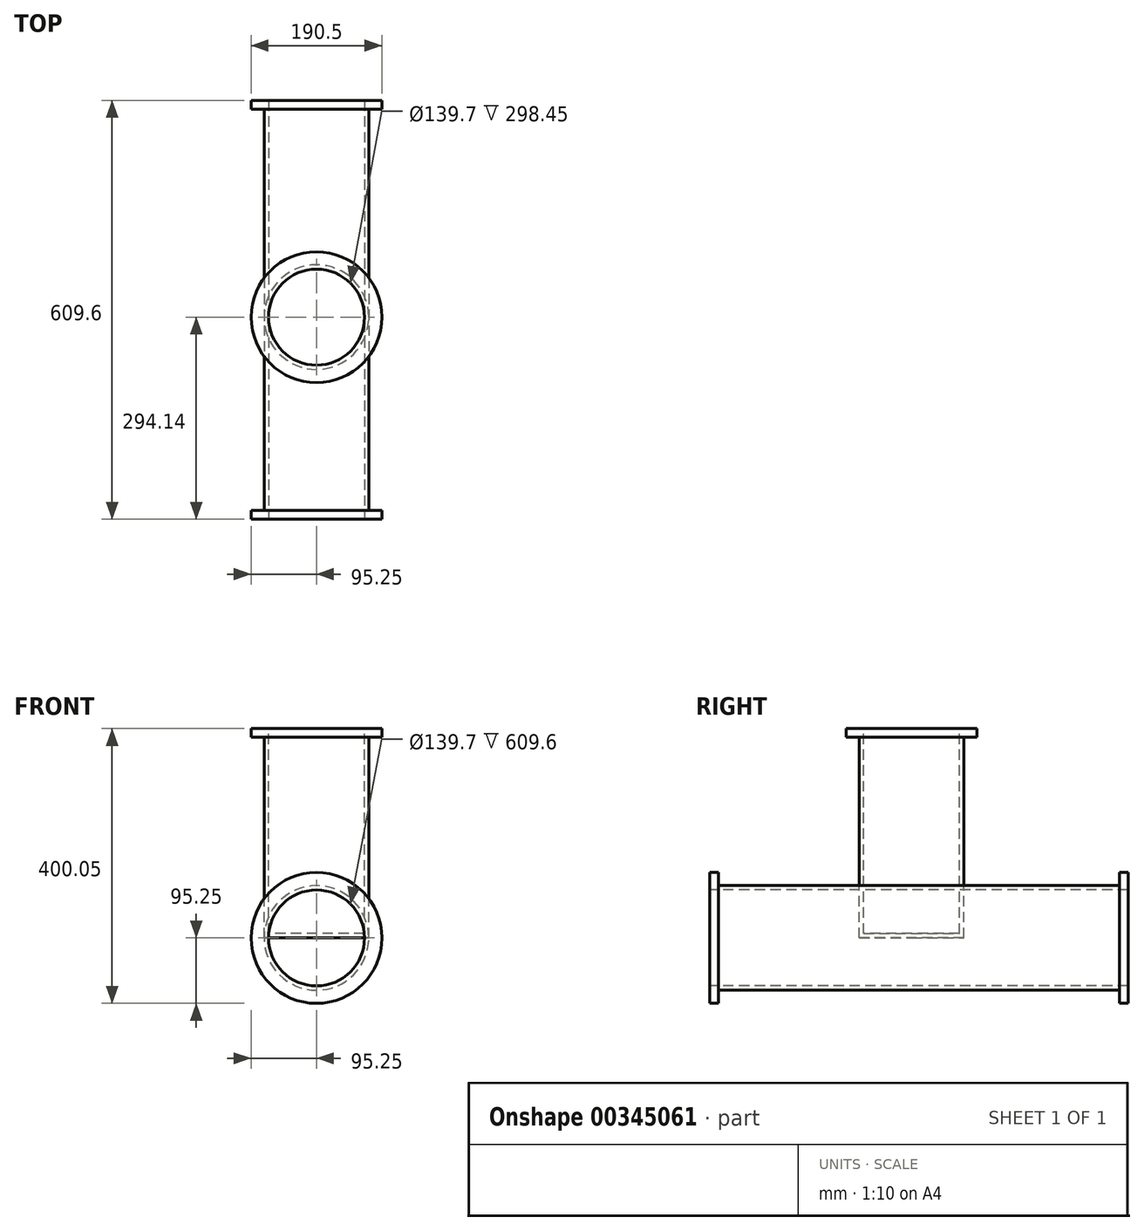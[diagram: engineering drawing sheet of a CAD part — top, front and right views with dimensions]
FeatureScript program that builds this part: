
annotation { "Feature Type Name" : "Feature", "Feature Type Description" : "" }
export const myFeature = defineFeature(function(context is Context, id is Id, definition is map)
    precondition{}
    {
        {
            var Q0;
            Q0=qCreatedBy(makeId("Right.planeOp"),FACE);
            var sketch = newSketch(context, id + "F0", { "sketchPlane" : qUnion([Q0])});
            skLineSegment(sketch, "E0", {"start": v(-294.14, 0) * mm, "end": v(315.46, 0) * mm});
            skLineSegment(sketch, "E1", {"start": v(0, 304.8) * mm, "end": v(0, 0) * mm});
            skSolve(sketch);
        }
        {
            var Q0;
            Q0=sQuery(id+"F0.wireOp",VERTEX,"E0.start");
            var Q1;
            Q1=qCreatedBy(makeId("Front.planeOp"),FACE);
            cPlane(context, id + "F1", {"entities" : qUnion([Q0, Q1]), "cplaneType" : CPlaneType.PLANE_POINT, "offset" : 320.04 * mm, "width" : 152.4 * mm, "height" : 152.4 * mm});
        }
        {
            var Q0;
            Q0=qCreatedBy(id+"F1.planeOp",FACE);
            var sketch = newSketch(context, id + "F2", { "sketchPlane" : qUnion([Q0])});
            skCircle(sketch, "E2", {"center": v(0, 0) * mm, "radius": 76.2 * mm});
            skSolve(sketch);
        }
        {
            var Q0;
            Q0=qCreatedBy(makeId("Top.planeOp"),FACE);
            var Q1;
            Q1=sQuery(id+"F0.wireOp",VERTEX,"E1.start");
            cPlane(context, id + "F3", {"entities" : qUnion([Q0, Q1]), "cplaneType" : CPlaneType.PLANE_POINT, "offset" : 25.4 * mm, "width" : 152.4 * mm, "height" : 152.4 * mm});
        }
        {
            var Q0;
            Q0=qCreatedBy(id+"F3.planeOp",FACE);
            var sketch = newSketch(context, id + "F4", { "sketchPlane" : qUnion([Q0])});
            skCircle(sketch, "E3", {"center": v(0, 0) * mm, "radius": 76.2 * mm});
            skSolve(sketch);
        }
        {
            var Q0;
            Q0=makeQuery(id+"F2.imprint","IMPRINT",FACE,{"disambiguationData":[TD([[makeQuery(id+"F2.imprint","IMPRINT",EDGE,{"derivedFrom":sQuery(id+"F2.wireOp",EDGE,"E2")}),1.0]])]});
            extrude(context, id + "F5", {"entities" : qUnion([Q0]), "oppositeDirection" : true, "depth" : 609.6 * mm});
        }
        {
            var Q0;
            Q0=makeQuery(id+"F4.imprint","IMPRINT",FACE,{"disambiguationData":[TD([[makeQuery(id+"F4.imprint","IMPRINT",EDGE,{"derivedFrom":sQuery(id+"F4.wireOp",EDGE,"E3")}),1.0]])]});
            extrude(context, id + "F6", {"entities" : qUnion([Q0]), "oppositeDirection" : true, "depth" : 304.8 * mm});
        }
        {
            var Q0;
            Q0=makeQuery(id+"F5.opExtrude","CAP_FACE",FACE,{"disambiguationData":[OSD([sQuery(id+"F2.wireOp",EDGE,"E2")])],"isStart":false});
            var Q1;
            Q1=makeQuery(id+"F6.opExtrude","CAP_FACE",FACE,{"disambiguationData":[OSD([sQuery(id+"F4.wireOp",EDGE,"E3")])],"isStart":true});
            var Q2;
            Q2=makeQuery(id+"F5.opExtrude","CAP_FACE",FACE,{"disambiguationData":[OSD([sQuery(id+"F2.wireOp",EDGE,"E2")])],"isStart":true});
            shell(context, id + "F7", {"entities" : qUnion([Q0, Q1, Q2]), "thickness" : 6.35 * mm});
        }
        {
            var Q0;
            Q0=sQuery(id+"F0.wireOp",EDGE,"E0");
            var Q1;
            Q1=sQuery(id+"F0.wireOp",VERTEX,"E0.start");
            cPlane(context, id + "F8", {"entities" : qUnion([Q0, Q1]), "cplaneType" : CPlaneType.LINE_POINT, "offset" : 25.4 * mm, "width" : 152.4 * mm, "height" : 152.4 * mm});
        }
        {
            var Q0;
            Q0=qCreatedBy(id+"F8.planeOp",FACE);
            var sketch = newSketch(context, id + "F9", { "sketchPlane" : qUnion([Q0])});
            skCircle(sketch, "E4", {"center": v(0, 0) * mm, "radius": 76.2 * mm});
            skCircle(sketch, "E5", {"center": v(0, 0) * mm, "radius": 95.25 * mm});
            skSolve(sketch);
        }
        {
            var Q0;
            Q0=makeQuery(id+"F9.imprint","IMPRINT",FACE,{"disambiguationData":[TD([[makeQuery(id+"F9.imprint","IMPRINT",EDGE,{"derivedFrom":sQuery(id+"F9.wireOp",EDGE,"E4")}),-1.0]])]});
            extrude(context, id + "F10", {"entities" : qUnion([Q0]), "operationType" : NewBodyOperationType.ADD, "depth" : 12.7 * mm});
        }
        {
            var Q0;
            Q0=sQuery(id+"F0.wireOp",EDGE,"E0");
            var Q1;
            Q1=sQuery(id+"F0.wireOp",VERTEX,"E0.end");
            cPlane(context, id + "F11", {"entities" : qUnion([Q0, Q1]), "cplaneType" : CPlaneType.LINE_POINT, "offset" : 25.4 * mm, "width" : 152.4 * mm, "height" : 152.4 * mm});
        }
        {
            var Q0;
            Q0=qCreatedBy(id+"F11.planeOp",FACE);
            var sketch = newSketch(context, id + "F12", { "sketchPlane" : qUnion([Q0])});
            skCircle(sketch, "E6", {"center": v(0, 0) * mm, "radius": 76.2 * mm});
            skCircle(sketch, "E7", {"center": v(0, 0) * mm, "radius": 95.25 * mm});
            skSolve(sketch);
        }
        {
            var Q0;
            Q0=makeQuery(id+"F12.imprint","IMPRINT",FACE,{"disambiguationData":[TD([[makeQuery(id+"F12.imprint","IMPRINT",EDGE,{"derivedFrom":sQuery(id+"F12.wireOp",EDGE,"E6")}),-1.0]])]});
            extrude(context, id + "F13", {"entities" : qUnion([Q0]), "operationType" : NewBodyOperationType.ADD, "depth" : -12.7 * mm});
        }
        {
            var Q0;
            Q0=qCreatedBy(id+"F3.planeOp",FACE);
            var sketch = newSketch(context, id + "F14", { "sketchPlane" : qUnion([Q0])});
            skCircle(sketch, "E8", {"center": v(0, 0) * mm, "radius": 76.2 * mm});
            skCircle(sketch, "E9", {"center": v(0, 0) * mm, "radius": 95.25 * mm});
            skSolve(sketch);
        }
        {
            var Q0;
            Q0=makeQuery(id+"F14.imprint","IMPRINT",FACE,{"disambiguationData":[TD([[makeQuery(id+"F14.imprint","IMPRINT",EDGE,{"derivedFrom":sQuery(id+"F14.wireOp",EDGE,"E8")}),-1.0]])]});
            extrude(context, id + "F15", {"entities" : qUnion([Q0]), "operationType" : NewBodyOperationType.ADD, "depth" : -12.7 * mm});
        }
    });
